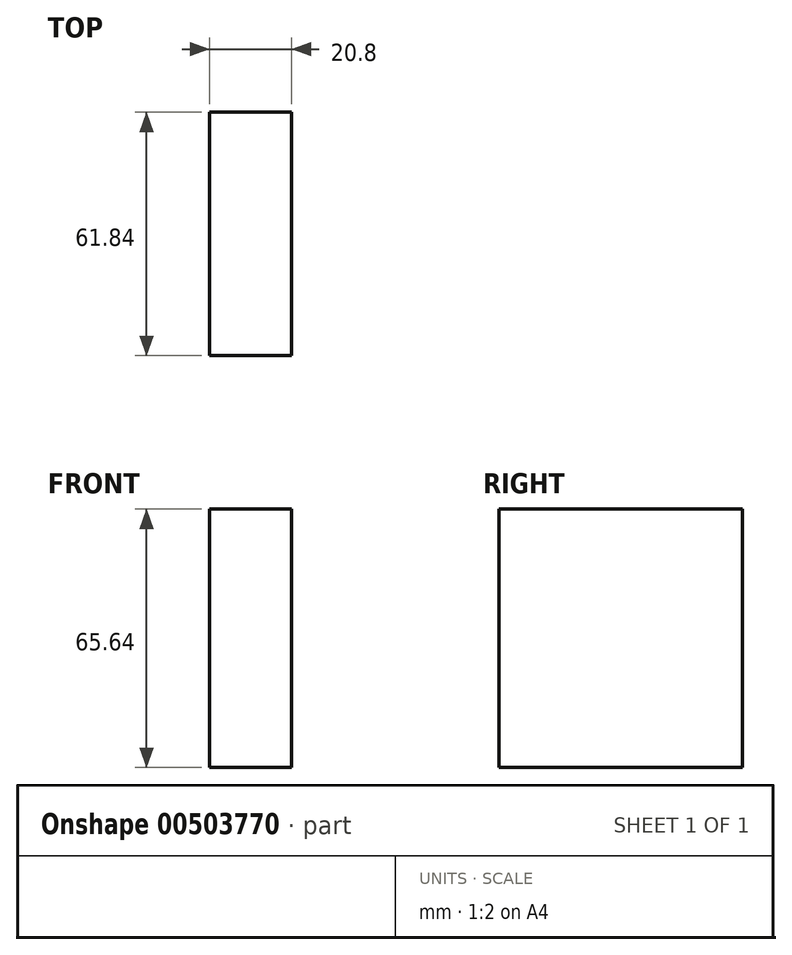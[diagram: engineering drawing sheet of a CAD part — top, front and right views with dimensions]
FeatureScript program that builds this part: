
annotation { "Feature Type Name" : "Feature", "Feature Type Description" : "" }
export const myFeature = defineFeature(function(context is Context, id is Id, definition is map)
    precondition{}
    {
        {
            var Q0;
            Q0=qCreatedBy(makeId("Right.planeOp"),FACE);
            var sketch = newSketch(context, id + "F0", { "sketchPlane" : qUnion([Q0])});
            skLineSegment(sketch, "E0.bottom", {"start": v(-37.95, 36.01) * mm, "end": v(23.9, 36.01) * mm});
            skLineSegment(sketch, "E0.top", {"start": v(-37.95, -29.63) * mm, "end": v(23.9, -29.63) * mm});
            skLineSegment(sketch, "E0.left", {"start": v(-37.95, 36.01) * mm, "end": v(-37.95, -29.63) * mm});
            skLineSegment(sketch, "E0.right", {"start": v(23.9, 36.01) * mm, "end": v(23.9, -29.63) * mm});
            skSolve(sketch);
        }
        {
            var Q0;
            Q0=makeQuery(id+"F0.imprint","IMPRINT",FACE,{"disambiguationData":[TD([[makeQuery(id+"F0.imprint","IMPRINT",EDGE,{"derivedFrom":sQuery(id+"F0.wireOp",EDGE,"E0.bottom")}),-1.0]])]});
            extrude(context, id + "F1", {"entities" : qUnion([Q0]), "depth" : 20.8 * mm, "offsetDistance" : 25 * mm});
        }
    });
